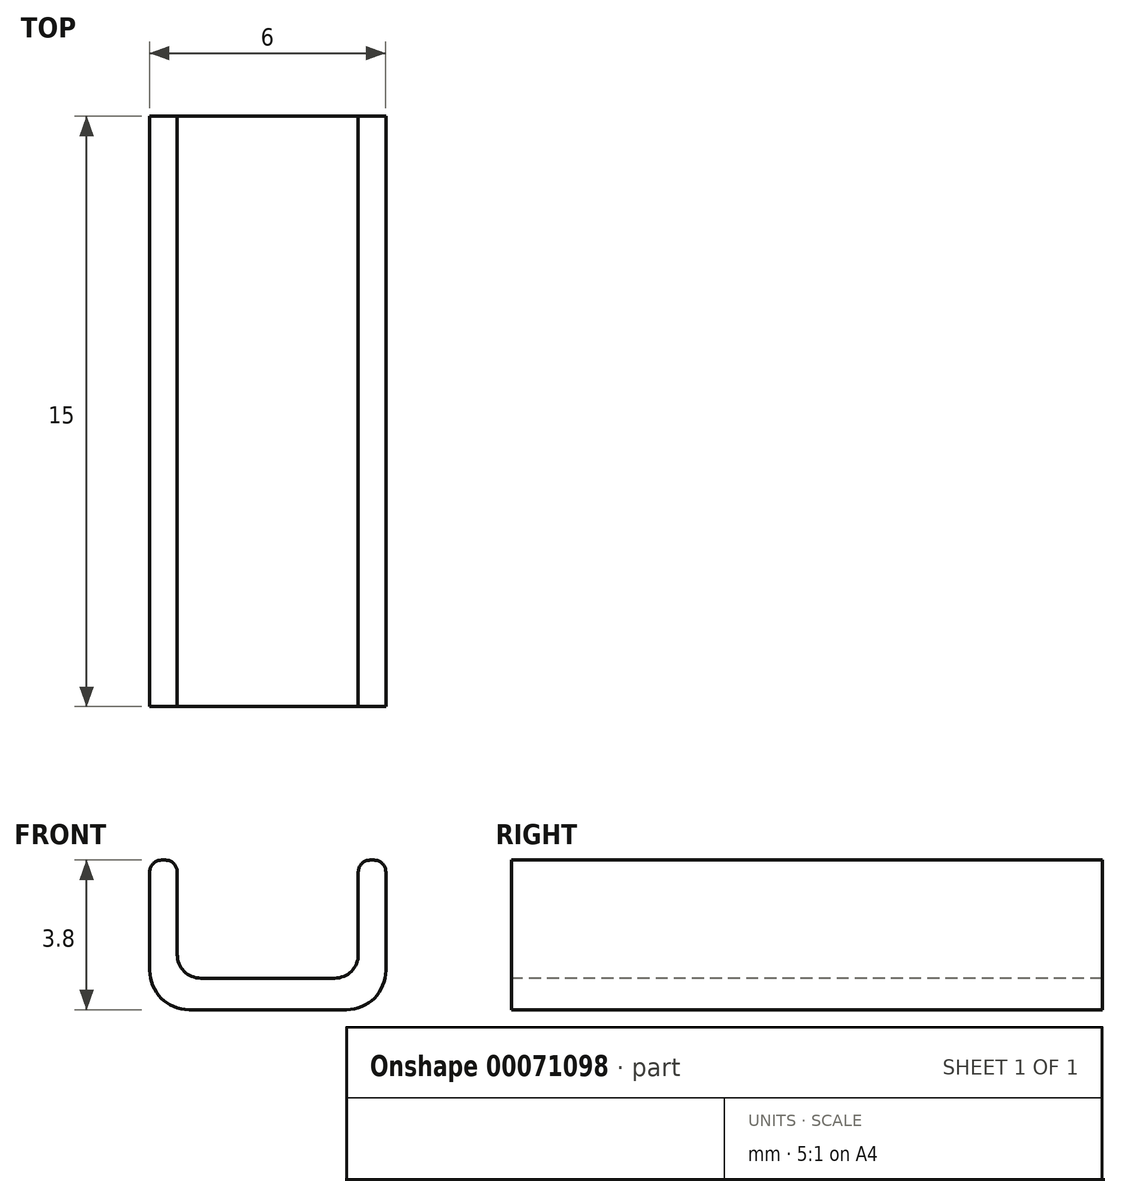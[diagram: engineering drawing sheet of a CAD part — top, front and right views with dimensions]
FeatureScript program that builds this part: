
annotation { "Feature Type Name" : "Feature", "Feature Type Description" : "" }
export const myFeature = defineFeature(function(context is Context, id is Id, definition is map)
    precondition{}
    {
        {
            var Q0;
            Q0=qCreatedBy(makeId("Front.planeOp"),FACE);
            var sketch = newSketch(context, id + "F0", { "sketchPlane" : qUnion([Q0])});
            skLineSegment(sketch, "E0.bottom", {"start": v(-2.88, 3.8) * mm, "end": v(-2.78, 3.8) * mm});
            skLineSegment(sketch, "E0.top", {"start": v(-2.18, 0) * mm, "end": v(1.82, 0) * mm});
            skLineSegment(sketch, "E0.left", {"start": v(-3.18, 3.5) * mm, "end": v(-3.18, 1) * mm});
            skLineSegment(sketch, "E0.right", {"start": v(2.82, 3.5) * mm, "end": v(2.82, 1) * mm});
            skLineSegment(sketch, "E1", {"start": v(-2.48, 3.5) * mm, "end": v(-2.48, 1.4) * mm});
            skLineSegment(sketch, "E2", {"start": v(-1.88, 0.8) * mm, "end": v(1.52, 0.8) * mm});
            skLineSegment(sketch, "E3", {"start": v(2.12, 1.4) * mm, "end": v(2.12, 3.5) * mm});
            skLineSegment(sketch, "E4", {"start": v(2.42, 3.8) * mm, "end": v(2.52, 3.8) * mm});
            skPoint(sketch, "E5.visualSharp", {"position": v(-2.48, 0.8) * mm});
            skArc(sketch, "E5.filletArc", {"start": v(-2.48, 1.4) * mm, "mid": v(-2.3, 0.98) * mm, "end": v(-1.88, 0.8) * mm});
            skPoint(sketch, "E6.visualSharp", {"position": v(2.12, 0.8) * mm});
            skArc(sketch, "E6.filletArc", {"start": v(1.52, 0.8) * mm, "mid": v(1.95, 0.98) * mm, "end": v(2.12, 1.4) * mm});
            skPoint(sketch, "E7.visualSharp", {"position": v(-2.48, 3.8) * mm});
            skArc(sketch, "E7.filletArc", {"start": v(-2.48, 3.5) * mm, "mid": v(-2.57, 3.71) * mm, "end": v(-2.78, 3.8) * mm});
            skPoint(sketch, "E8.visualSharp", {"position": v(-3.18, 3.8) * mm});
            skArc(sketch, "E8.filletArc", {"start": v(-2.88, 3.8) * mm, "mid": v(-3.1, 3.71) * mm, "end": v(-3.18, 3.5) * mm});
            skPoint(sketch, "E9.visualSharp", {"position": v(2.12, 3.8) * mm});
            skArc(sketch, "E9.filletArc", {"start": v(2.42, 3.8) * mm, "mid": v(2.2, 3.71) * mm, "end": v(2.12, 3.5) * mm});
            skPoint(sketch, "E10.visualSharp", {"position": v(2.82, 3.8) * mm});
            skArc(sketch, "E10.filletArc", {"start": v(2.82, 3.5) * mm, "mid": v(2.73, 3.71) * mm, "end": v(2.52, 3.8) * mm});
            skPoint(sketch, "E11.visualSharp", {"position": v(-3.18, 0) * mm});
            skArc(sketch, "E11.filletArc", {"start": v(-3.18, 1) * mm, "mid": v(-2.89, 0.3) * mm, "end": v(-2.18, 0) * mm});
            skPoint(sketch, "E12.visualSharp", {"position": v(2.82, 0) * mm});
            skArc(sketch, "E12.filletArc", {"start": v(1.82, 0) * mm, "mid": v(2.53, 0.3) * mm, "end": v(2.82, 1) * mm});
            skSolve(sketch);
        }
        {
            var Q0;
            Q0=makeQuery(id+"F0.imprint","IMPRINT",FACE,{"disambiguationData":[TD([[makeQuery(id+"F0.imprint","IMPRINT",EDGE,{"derivedFrom":sQuery(id+"F0.wireOp",EDGE,"E0.bottom")}),-1.0]])]});
            extrude(context, id + "F1", {"entities" : qUnion([Q0]), "oppositeDirection" : true, "depth" : 15 * mm});
        }
    });
